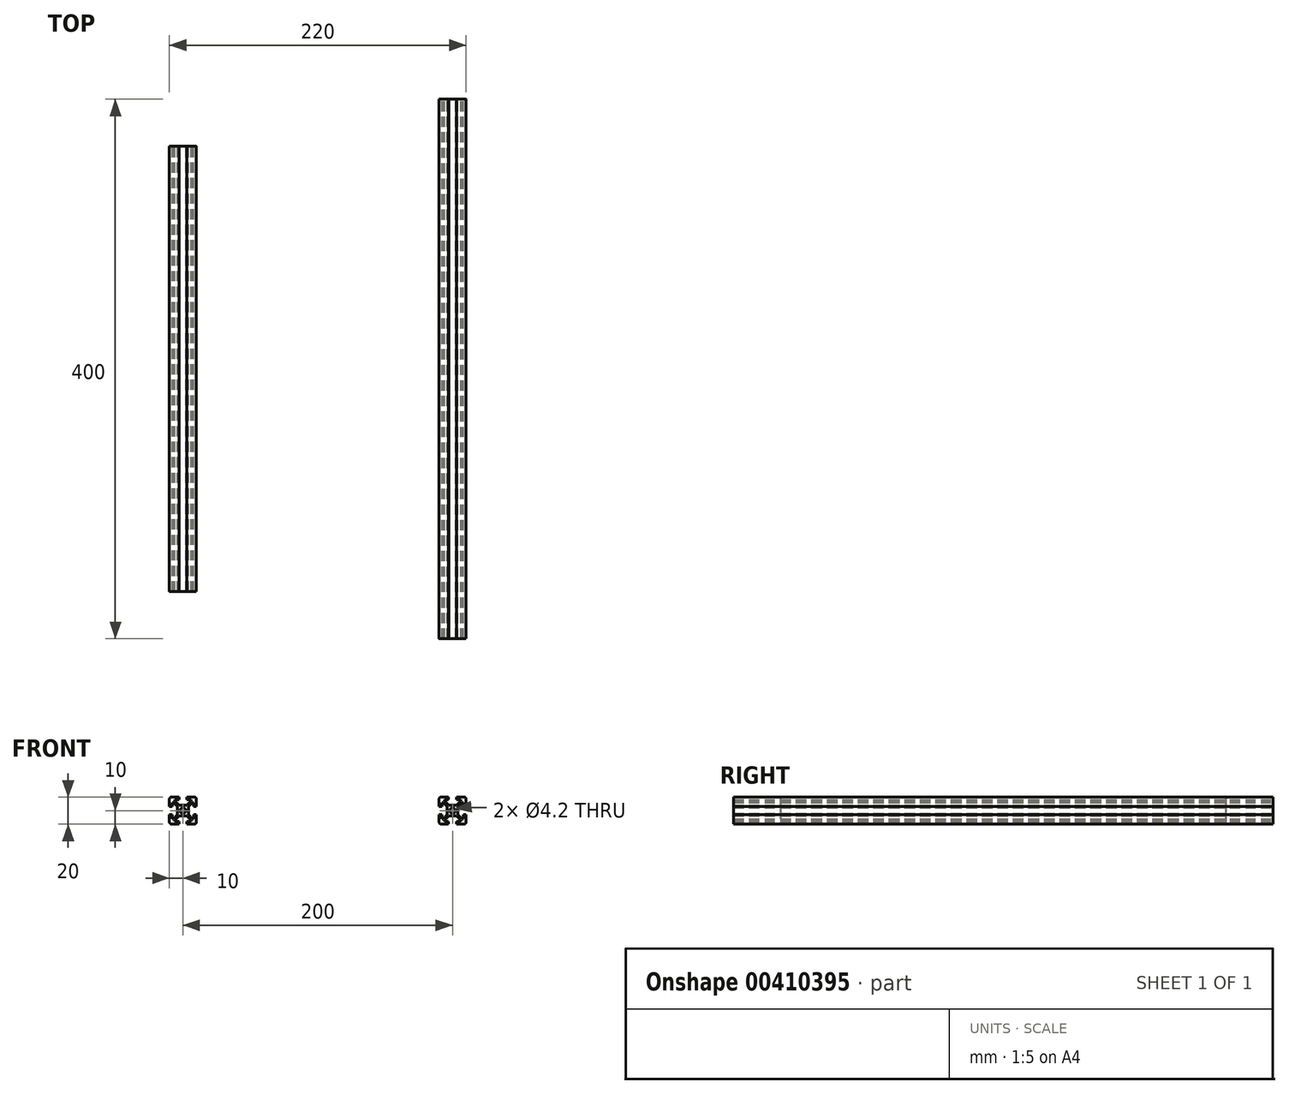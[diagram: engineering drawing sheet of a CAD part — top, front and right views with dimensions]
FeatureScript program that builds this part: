
annotation { "Feature Type Name" : "Feature", "Feature Type Description" : "" }
export const myFeature = defineFeature(function(context is Context, id is Id, definition is map)
    precondition{}
    {
        {
            var Q0;
            Q0=qCreatedBy(makeId("Front.planeOp"),FACE);
            var sketch = newSketch(context, id + "F0", { "sketchPlane" : qUnion([Q0])});
            skLineSegment(sketch, "E0", {"start": v(0, 0) * mm, "end": v(0, 4) * mm, "construction": true});
            skLineSegment(sketch, "E1", {"start": v(-2.94, 4) * mm, "end": v(2.94, 4) * mm});
            skLineSegment(sketch, "E2", {"start": v(0, 0) * mm, "end": v(10, 10) * mm, "construction": true});
            skLineSegment(sketch, "E3", {"start": v(10, 10) * mm, "end": v(-10, 10) * mm, "construction": true});
            skLineSegment(sketch, "E4", {"start": v(-10, 10) * mm, "end": v(0, 0) * mm, "construction": true});
            skLineSegment(sketch, "E5", {"start": v(-10, 10) * mm, "end": v(-3, 10) * mm});
            skLineSegment(sketch, "E6", {"start": v(-3, 10) * mm, "end": v(-3, 8) * mm});
            skLineSegment(sketch, "E7", {"start": v(-3, 8) * mm, "end": v(-6, 8) * mm});
            skLineSegment(sketch, "E8", {"start": v(-6, 8) * mm, "end": v(-6, 7.06) * mm});
            skLineSegment(sketch, "E9", {"start": v(-6, 7.06) * mm, "end": v(-2.94, 4) * mm});
            skLineSegment(sketch, "E10", {"start": v(2.94, 4) * mm, "end": v(6, 7.06) * mm});
            skLineSegment(sketch, "E11", {"start": v(6, 7.06) * mm, "end": v(6, 8) * mm});
            skLineSegment(sketch, "E12", {"start": v(6, 8) * mm, "end": v(3, 8) * mm});
            skLineSegment(sketch, "E13", {"start": v(3, 8) * mm, "end": v(3, 10) * mm});
            skLineSegment(sketch, "E14", {"start": v(3, 10) * mm, "end": v(10, 10) * mm});
            skLineSegment(sketch, "E15.0.MirrorCS", {"start": v(-10, -3) * mm, "end": v(-10, -10) * mm});
            skLineSegment(sketch, "E15.1.MirrorCS", {"start": v(-7.06, -6) * mm, "end": v(-8, -6) * mm});
            skLineSegment(sketch, "E15.2.MirrorCS", {"start": v(-8, -6) * mm, "end": v(-8, -3) * mm});
            skLineSegment(sketch, "E15.3.MirrorCS", {"start": v(-8, -3) * mm, "end": v(-10, -3) * mm});
            skLineSegment(sketch, "E15.4.MirrorCS", {"start": v(-10, 10) * mm, "end": v(-10, 3) * mm});
            skLineSegment(sketch, "E15.5.MirrorCS", {"start": v(-10, 3) * mm, "end": v(-8, 3) * mm});
            skLineSegment(sketch, "E15.6.MirrorCS", {"start": v(-8, 3) * mm, "end": v(-8, 6) * mm});
            skLineSegment(sketch, "E15.7.MirrorCS", {"start": v(-8, 6) * mm, "end": v(-7.06, 6) * mm});
            skLineSegment(sketch, "E15.8.MirrorCS", {"start": v(-7.06, 6) * mm, "end": v(-4, 2.94) * mm});
            skLineSegment(sketch, "E15.9.MirrorCS", {"start": v(-4, -2.94) * mm, "end": v(-7.06, -6) * mm});
            skLineSegment(sketch, "E15.10.MirrorCS", {"start": v(-4, 2.94) * mm, "end": v(-4, -2.94) * mm});
            skLineSegment(sketch, "E16", {"start": v(-10, -10) * mm, "end": v(0, 0) * mm, "construction": true});
            skLineSegment(sketch, "E17", {"start": v(-10, 10) * mm, "end": v(-10, -10) * mm, "construction": true});
            skLineSegment(sketch, "E18.0.MirrorCS", {"start": v(10, 3) * mm, "end": v(10, 10) * mm});
            skLineSegment(sketch, "E18.1.MirrorCS", {"start": v(8, 3) * mm, "end": v(10, 3) * mm});
            skLineSegment(sketch, "E18.2.MirrorCS", {"start": v(8, 6) * mm, "end": v(8, 3) * mm});
            skLineSegment(sketch, "E18.3.MirrorCS", {"start": v(7.06, 6) * mm, "end": v(8, 6) * mm});
            skLineSegment(sketch, "E18.4.MirrorCS", {"start": v(4, 2.94) * mm, "end": v(7.06, 6) * mm});
            skLineSegment(sketch, "E18.5.MirrorCS", {"start": v(4, -2.94) * mm, "end": v(4, 2.94) * mm});
            skLineSegment(sketch, "E18.6.MirrorCS", {"start": v(7.06, -6) * mm, "end": v(4, -2.94) * mm});
            skLineSegment(sketch, "E18.7.MirrorCS", {"start": v(8, -6) * mm, "end": v(7.06, -6) * mm});
            skLineSegment(sketch, "E18.8.MirrorCS", {"start": v(8, -3) * mm, "end": v(8, -6) * mm});
            skLineSegment(sketch, "E18.9.MirrorCS", {"start": v(10, -3) * mm, "end": v(8, -3) * mm});
            skLineSegment(sketch, "E18.10.MirrorCS", {"start": v(10, -10) * mm, "end": v(10, -3) * mm});
            skLineSegment(sketch, "E18.11.MirrorCS", {"start": v(10, -10) * mm, "end": v(3, -10) * mm});
            skLineSegment(sketch, "E18.12.MirrorCS", {"start": v(3, -10) * mm, "end": v(3, -8) * mm});
            skLineSegment(sketch, "E18.13.MirrorCS", {"start": v(3, -8) * mm, "end": v(6, -8) * mm});
            skLineSegment(sketch, "E18.14.MirrorCS", {"start": v(6, -8) * mm, "end": v(6, -7.06) * mm});
            skLineSegment(sketch, "E18.15.MirrorCS", {"start": v(6, -7.06) * mm, "end": v(2.94, -4) * mm});
            skLineSegment(sketch, "E18.16.MirrorCS", {"start": v(2.94, -4) * mm, "end": v(-2.94, -4) * mm});
            skLineSegment(sketch, "E18.17.MirrorCS", {"start": v(-2.94, -4) * mm, "end": v(-6, -7.06) * mm});
            skLineSegment(sketch, "E18.18.MirrorCS", {"start": v(-6, -7.06) * mm, "end": v(-6, -8) * mm});
            skLineSegment(sketch, "E18.19.MirrorCS", {"start": v(-6, -8) * mm, "end": v(-3, -8) * mm});
            skLineSegment(sketch, "E18.20.MirrorCS", {"start": v(-3, -10) * mm, "end": v(-10, -10) * mm});
            skLineSegment(sketch, "E18.21.MirrorCS", {"start": v(-3, -8) * mm, "end": v(-3, -10) * mm});
            skLineSegment(sketch, "E19", {"start": v(0, 0) * mm, "end": v(10, -10) * mm, "construction": true});
            skLineSegment(sketch, "E20", {"start": v(10, -10) * mm, "end": v(-10, -10) * mm, "construction": true});
            skLineSegment(sketch, "E21", {"start": v(10, 10) * mm, "end": v(10, -10) * mm, "construction": true});
            skCircle(sketch, "E22", {"center": v(0, 0) * mm, "radius": 2.1 * mm});
            skSolve(sketch);
        }
        {
            var Q0;
            Q0=makeQuery(id+"F0.imprint","IMPRINT",FACE,{"disambiguationData":[TD([[makeQuery(id+"F0.imprint","IMPRINT",EDGE,{"derivedFrom":sQuery(id+"F0.wireOp",EDGE,"E1")}),-1.0]])]});
            extrude(context, id + "F1", {"entities" : qUnion([Q0]), "endBound" : BoundingType.SYMMETRIC, "depth" : 400 * mm});
        }
        {
            var Q0;
            Q0=makeQuery(id+"F1.opExtrude","SWEPT_EDGE",EDGE,{"disambiguationData":[OSD([sQuery(id+"F0.wireOp",EDGE,"E18.10.MirrorCS"),sQuery(id+"F0.wireOp",EDGE,"E18.11.MirrorCS")])]});
            var Q1;
            Q1=makeQuery(id+"F1.opExtrude","SWEPT_EDGE",EDGE,{"disambiguationData":[OSD([sQuery(id+"F0.wireOp",EDGE,"E14"),sQuery(id+"F0.wireOp",EDGE,"E18.0.MirrorCS")])]});
            var Q2;
            Q2=makeQuery(id+"F1.opExtrude","SWEPT_EDGE",EDGE,{"disambiguationData":[OSD([sQuery(id+"F0.wireOp",EDGE,"E5"),sQuery(id+"F0.wireOp",EDGE,"E15.4.MirrorCS")])]});
            var Q3;
            Q3=makeQuery(id+"F1.opExtrude","SWEPT_EDGE",EDGE,{"disambiguationData":[OSD([sQuery(id+"F0.wireOp",EDGE,"E15.0.MirrorCS"),sQuery(id+"F0.wireOp",EDGE,"E18.20.MirrorCS")])]});
            fillet(context, id + "F2", {"entities" : qUnion([Q0, Q1, Q2, Q3]), "radius" : 1.5 * mm, "tangentPropagation" : true, "allowEdgeOverflow" : false});
        }
        {
            var Q0;
            Q0=makeQuery(id+"F1.opExtrude","SWEPT_BODY",BODY,{"disambiguationData":[OSD([sQuery(id+"F0.wireOp",EDGE,"E1"),sQuery(id+"F0.wireOp",EDGE,"E5"),sQuery(id+"F0.wireOp",EDGE,"E6"),sQuery(id+"F0.wireOp",EDGE,"E7"),sQuery(id+"F0.wireOp",EDGE,"E8"),sQuery(id+"F0.wireOp",EDGE,"E9"),sQuery(id+"F0.wireOp",EDGE,"E10"),sQuery(id+"F0.wireOp",EDGE,"E11"),sQuery(id+"F0.wireOp",EDGE,"E12"),sQuery(id+"F0.wireOp",EDGE,"E13"),sQuery(id+"F0.wireOp",EDGE,"E14"),sQuery(id+"F0.wireOp",EDGE,"E15.0.MirrorCS"),sQuery(id+"F0.wireOp",EDGE,"E15.1.MirrorCS"),sQuery(id+"F0.wireOp",EDGE,"E15.2.MirrorCS"),sQuery(id+"F0.wireOp",EDGE,"E15.3.MirrorCS"),sQuery(id+"F0.wireOp",EDGE,"E15.4.MirrorCS"),sQuery(id+"F0.wireOp",EDGE,"E15.5.MirrorCS"),sQuery(id+"F0.wireOp",EDGE,"E15.6.MirrorCS"),sQuery(id+"F0.wireOp",EDGE,"E15.7.MirrorCS"),sQuery(id+"F0.wireOp",EDGE,"E15.8.MirrorCS"),sQuery(id+"F0.wireOp",EDGE,"E15.9.MirrorCS"),sQuery(id+"F0.wireOp",EDGE,"E15.10.MirrorCS"),sQuery(id+"F0.wireOp",EDGE,"E18.0.MirrorCS"),sQuery(id+"F0.wireOp",EDGE,"E18.1.MirrorCS"),sQuery(id+"F0.wireOp",EDGE,"E18.2.MirrorCS"),sQuery(id+"F0.wireOp",EDGE,"E18.3.MirrorCS"),sQuery(id+"F0.wireOp",EDGE,"E18.4.MirrorCS"),sQuery(id+"F0.wireOp",EDGE,"E18.5.MirrorCS"),sQuery(id+"F0.wireOp",EDGE,"E18.6.MirrorCS"),sQuery(id+"F0.wireOp",EDGE,"E18.7.MirrorCS"),sQuery(id+"F0.wireOp",EDGE,"E18.8.MirrorCS"),sQuery(id+"F0.wireOp",EDGE,"E18.9.MirrorCS"),sQuery(id+"F0.wireOp",EDGE,"E18.10.MirrorCS"),sQuery(id+"F0.wireOp",EDGE,"E18.11.MirrorCS"),sQuery(id+"F0.wireOp",EDGE,"E18.12.MirrorCS"),sQuery(id+"F0.wireOp",EDGE,"E18.13.MirrorCS"),sQuery(id+"F0.wireOp",EDGE,"E18.14.MirrorCS"),sQuery(id+"F0.wireOp",EDGE,"E18.15.MirrorCS"),sQuery(id+"F0.wireOp",EDGE,"E18.16.MirrorCS"),sQuery(id+"F0.wireOp",EDGE,"E18.17.MirrorCS"),sQuery(id+"F0.wireOp",EDGE,"E18.18.MirrorCS"),sQuery(id+"F0.wireOp",EDGE,"E18.19.MirrorCS"),sQuery(id+"F0.wireOp",EDGE,"E18.20.MirrorCS"),sQuery(id+"F0.wireOp",EDGE,"E18.21.MirrorCS"),sQuery(id+"F0.wireOp",EDGE,"E22")])]});
            transform(context, id + "F3", {"entities" : qUnion([Q0]), "transformType" : TransformType.TRANSLATION_3D, "dx" : 200 * mm, "dy" : 0 * mm, "dz" : 0 * mm, "makeCopy" : false});
        }
        {
            var Q0;
            Q0=makeQuery(id+"F0.imprint","IMPRINT",FACE,{"disambiguationData":[TD([[makeQuery(id+"F0.imprint","IMPRINT",EDGE,{"derivedFrom":sQuery(id+"F0.wireOp",EDGE,"E1")}),-1.0]])]});
            extrude(context, id + "F4", {"entities" : qUnion([Q0]), "endBound" : BoundingType.SYMMETRIC, "depth" : 330 * mm});
        }
        {
            var Q0;
            Q0=makeQuery(id+"F4.opExtrude","SWEPT_EDGE",EDGE,{"disambiguationData":[OSD([sQuery(id+"F0.wireOp",EDGE,"E14"),sQuery(id+"F0.wireOp",EDGE,"E18.0.MirrorCS")])]});
            var Q1;
            Q1=makeQuery(id+"F4.opExtrude","SWEPT_EDGE",EDGE,{"disambiguationData":[OSD([sQuery(id+"F0.wireOp",EDGE,"E5"),sQuery(id+"F0.wireOp",EDGE,"E15.4.MirrorCS")])]});
            var Q2;
            Q2=makeQuery(id+"F4.opExtrude","SWEPT_EDGE",EDGE,{"disambiguationData":[OSD([sQuery(id+"F0.wireOp",EDGE,"E18.10.MirrorCS"),sQuery(id+"F0.wireOp",EDGE,"E18.11.MirrorCS")])]});
            var Q3;
            Q3=makeQuery(id+"F4.opExtrude","SWEPT_EDGE",EDGE,{"disambiguationData":[OSD([sQuery(id+"F0.wireOp",EDGE,"E15.0.MirrorCS"),sQuery(id+"F0.wireOp",EDGE,"E18.20.MirrorCS")])]});
            fillet(context, id + "F5", {"entities" : qUnion([Q0, Q1, Q2, Q3]), "radius" : 1.5 * mm, "tangentPropagation" : true, "allowEdgeOverflow" : false});
        }
    });
